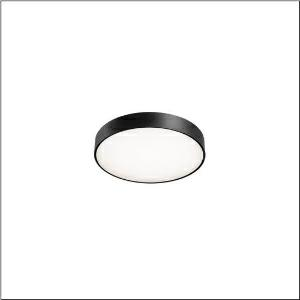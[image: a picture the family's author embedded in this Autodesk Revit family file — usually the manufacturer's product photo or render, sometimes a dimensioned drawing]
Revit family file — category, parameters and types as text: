
# Revit family: round_21_s_51mr34gd0321b
name_source: partatom
category: Lighting Fixtures
units: mm (PartAtom-declared; Revit-internal decimal feet)

## family parameters
Cut with Voids When Loaded = No
Host = Face
Light Source = No
Part Type = Normal
Room Calculation Point = No
Round Connector Dimension = Use Diameter
Shared = No

## types (1)
- Round 21 S (1 x LED, 3930 lm, 28.3 W, 3000K)
    Apparent Load = 28 VA
    CIE Flux Codes = 49 80 96 79 100
    Color Rendering = 80
    Color Temperature = 3000K
    Default Elevation = 1800 mm
    Description = Round 21 S, wall and ceiling luminaire, primary optical cover: cover, of PMMA, opal, light emission: direct/indirect distribution, primary light characteristic: symmetric, installation type: suspended mounting, surface-mounted, LED, rated luminous flux: 3.930lm, luminous efficacy: 139lm/W, light colour: 830, colour temperature: 3000K, control gear: DALI 2, with terminal, 5-pole, mains connection: 230V, AC, 50/60Hz, rated input power: 28.3W, housing, of aluminium, coated, black, diameter: 400mm, height: 62mm, protection rating (complete): IP40, insulation class (complete): insulation class I (protective earthing), certification: CE, impact resistance: IK04, permissible operating ambient temperature: -10..+35°C, packaging unit: 1 piece
    Height = 87 mm
    Lamp = 1 x LED
    Lamp Light Flux = 3930 lm
    Lamp Power = 28.3 W
    Lamp count = 1
    Length = 400 mm
    Luminous efficacy = 139 lm/W
    Manufacturer = Siteco
    ModVariant = No
    Model = 51MR34GD0321B
    Mounting Place = Ceiling
    Mounting Type = Surface mounted
    Number of Poles = 1
    OnlyDefault = Yes
    Power Factor = 1
    Product Name = Round 21 S
    Product group = wall and ceiling luminaire | ceiling mounted
    ProductGroupID = 304
    Protection Class = Protection class I
    Protection Degree = IP 40
    RLX_Detail_Level = 1
    RLX_Emergency_Light_Flux = 0 lm
    RLX_Emergency_Type = 0
    RLX_Emergency_Type_DB = No
    RlxData = <blob elided: 13877 chars, md5=efafc2cb>
    Socket = socket
    Standby Power = 0 W
    System Light Flux = 3930 lm
    System Power = 28 W
    Type Comments = Product without accessories
    Type Image = l_1258311.jpg
    URL = http://relux.com
    VarID = ---
    Voltage = 0 V
    Weight = 0.00 kg
    Width = 0 mm  [stored 0 ft]

note: [stored X ft] marks values corroborated as IEEE doubles in the binary element streams (Revit-internal decimal feet)

## geometry (parser evidence)
native form markers: Sweep x13
no freeform markers — native parametric forms only
